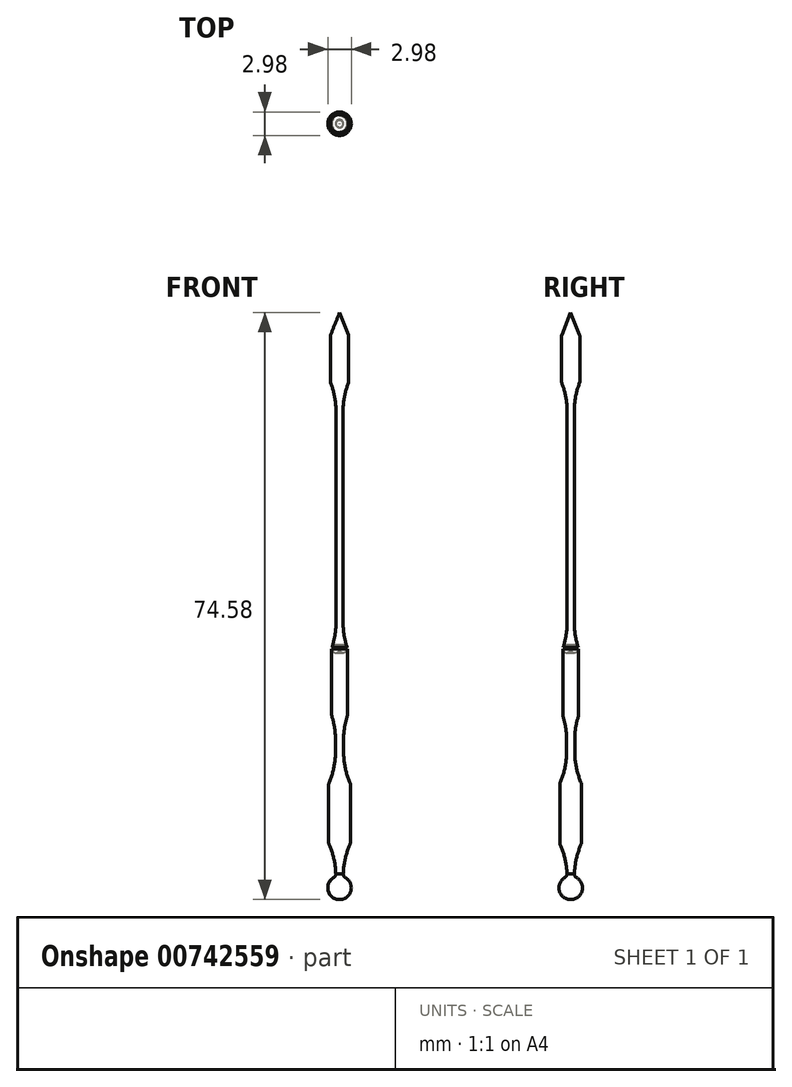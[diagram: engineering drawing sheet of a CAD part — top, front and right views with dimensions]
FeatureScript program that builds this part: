
annotation { "Feature Type Name" : "Feature", "Feature Type Description" : "" }
export const myFeature = defineFeature(function(context is Context, id is Id, definition is map)
    precondition{}
    {
        {
            var Q0;
            Q0=qCreatedBy(makeId("Front.planeOp"),FACE);
            var sketch = newSketch(context, id + "F0", { "sketchPlane" : qUnion([Q0])});
            skLineSegment(sketch, "E0", {"start": v(0, 9.94) * mm, "end": v(0.59, 8.47) * mm});
            skLineSegment(sketch, "E1", {"start": v(0.59, 8.47) * mm, "end": v(0.59, 5.32) * mm});
            skLineSegment(sketch, "E2", {"start": v(0.59, 5.32) * mm, "end": v(0.23, 5.32) * mm});
            skLineSegment(sketch, "E3", {"start": v(0.23, 5.32) * mm, "end": v(0.23, -11.17) * mm});
            skLineSegment(sketch, "E4", {"start": v(0.23, -11.17) * mm, "end": v(0.5, -11.17) * mm});
            skLineSegment(sketch, "E5", {"start": v(0.5, -11.17) * mm, "end": v(0.5, -15.88) * mm});
            skLineSegment(sketch, "E6", {"start": v(0.5, -15.88) * mm, "end": v(0.26, -15.88) * mm});
            skLineSegment(sketch, "E7", {"start": v(0.26, -15.88) * mm, "end": v(0.26, -19.8) * mm});
            skLineSegment(sketch, "E8", {"start": v(0.26, -19.8) * mm, "end": v(0.7, -19.8) * mm});
            skLineSegment(sketch, "E9", {"start": v(0.7, -19.8) * mm, "end": v(0.7, -23.98) * mm});
            skLineSegment(sketch, "E10", {"start": v(0.7, -23.98) * mm, "end": v(0.26, -23.98) * mm});
            skLineSegment(sketch, "E11", {"start": v(0.26, -23.98) * mm, "end": v(0.24, -25.9) * mm});
            skLineSegment(sketch, "E12", {"start": v(0, -26.6) * mm, "end": v(0, 9.94) * mm});
            skArc(sketch, "E13", {"start": v(0.24, -25.9) * mm, "mid": v(0.74, -26.72) * mm, "end": v(0, -27.35) * mm});
            skLineSegment(sketch, "E14", {"start": v(0, -26.6) * mm, "end": v(0, -27.35) * mm});
            skPoint(sketch, "E15.start.orphan", {"position": v(0.23, -26.6) * mm});
            skLineSegment(sketch, "E16", {"start": v(0, 9.94) * mm, "end": v(0, 12.06) * mm, "construction": true});
            skSolve(sketch);
        }
        {
            var Q0;
            Q0=makeQuery(id+"F0.imprint","IMPRINT",FACE,{"disambiguationData":[TD([[makeQuery(id+"F0.imprint","IMPRINT",EDGE,{"derivedFrom":sQuery(id+"F0.wireOp",EDGE,"E0")}),-1.0]])]});
            var Q1;
            Q1=sQuery(id+"F0.wireOp",EDGE,"E16");
            revolve(context, id + "F1", {"surfaceOperationType" : NewSurfaceOperationType.NEW, "entities" : qUnion([Q0]), "axis" : qUnion([Q1]), "revolveType" : RevolveType.FULL});
        }
        {
            var Q0;
            Q0=makeQuery(id+"F1.opRevolve","SWEPT_EDGE",EDGE,{"disambiguationData":[OSD([sQuery(id+"F0.wireOp",EDGE,"E1"),sQuery(id+"F0.wireOp",EDGE,"E2")])]});
            var Q1;
            Q1=makeQuery(id+"F1.opRevolve","SWEPT_EDGE",EDGE,{"disambiguationData":[OSD([sQuery(id+"F0.wireOp",EDGE,"E0"),sQuery(id+"F0.wireOp",EDGE,"E1")])]});
            var Q2;
            Q2=makeQuery(id+"F1.opRevolve","SWEPT_EDGE",EDGE,{"disambiguationData":[OSD([sQuery(id+"F0.wireOp",EDGE,"E4"),sQuery(id+"F0.wireOp",EDGE,"E5")])]});
            var Q3;
            Q3=makeQuery(id+"F1.opRevolve","SWEPT_EDGE",EDGE,{"disambiguationData":[OSD([sQuery(id+"F0.wireOp",EDGE,"E5"),sQuery(id+"F0.wireOp",EDGE,"E6")])]});
            var Q4;
            Q4=makeQuery(id+"F1.opRevolve","SWEPT_EDGE",EDGE,{"disambiguationData":[OSD([sQuery(id+"F0.wireOp",EDGE,"E8"),sQuery(id+"F0.wireOp",EDGE,"E9")])]});
            var Q5;
            Q5=makeQuery(id+"F1.opRevolve","SWEPT_EDGE",EDGE,{"disambiguationData":[OSD([sQuery(id+"F0.wireOp",EDGE,"E9"),sQuery(id+"F0.wireOp",EDGE,"E10")])]});
            var Q6;
            Q6=makeQuery(id+"F1.opRevolve","SWEPT_EDGE",EDGE,{"disambiguationData":[OSD([sQuery(id+"F0.wireOp",EDGE,"E11"),sQuery(id+"F0.wireOp",EDGE,"E13")])]});
            fillet(context, id + "F2", {"entities" : qUnion([Q0, Q1, Q2, Q3, Q4, Q5, Q6]), "radius" : 0.25 * mm, "tangentPropagation" : true, "allowEdgeOverflow" : false});
        }
        {
            var Q0;
            Q0=makeQuery(id+"F1.opRevolve","SWEPT_EDGE",EDGE,{"disambiguationData":[OSD([sQuery(id+"F0.wireOp",EDGE,"E10"),sQuery(id+"F0.wireOp",EDGE,"E11")])]});
            var Q1;
            Q1=makeQuery(id+"F1.opRevolve","SWEPT_EDGE",EDGE,{"disambiguationData":[OSD([sQuery(id+"F0.wireOp",EDGE,"E7"),sQuery(id+"F0.wireOp",EDGE,"E8")])]});
            var Q2;
            Q2=makeQuery(id+"F2.opFillet","BLEND_EDGE",EDGE,{"blendedFrom":[makeQuery(id+"F1.opRevolve","SWEPT_EDGE",EDGE,{"disambiguationData":[OSD([sQuery(id+"F0.wireOp",EDGE,"E5"),sQuery(id+"F0.wireOp",EDGE,"E6")])]}),makeQuery(id+"F1.opRevolve","SWEPT_FACE",FACE,{"disambiguationData":[OSD([sQuery(id+"F0.wireOp",EDGE,"E7")])]})],"blendedInto":[makeQuery(id+"F1.opRevolve","SWEPT_FACE",FACE,{"disambiguationData":[OSD([sQuery(id+"F0.wireOp",EDGE,"E7")])]})]});
            var Q3;
            Q3=makeQuery(id+"F1.opRevolve","SWEPT_EDGE",EDGE,{"disambiguationData":[OSD([sQuery(id+"F0.wireOp",EDGE,"E3"),sQuery(id+"F0.wireOp",EDGE,"E4")])]});
            var Q4;
            Q4=makeQuery(id+"F1.opRevolve","SWEPT_EDGE",EDGE,{"disambiguationData":[OSD([sQuery(id+"F0.wireOp",EDGE,"E2"),sQuery(id+"F0.wireOp",EDGE,"E3")])]});
            fillet(context, id + "F3", {"entities" : qUnion([Q0, Q1, Q2, Q3, Q4]), "radius" : 5.08 * mm, "tangentPropagation" : true, "allowEdgeOverflow" : false});
        }
        {
            var Q0;
            Q0=makeQuery(id+"F1.opRevolve","SWEPT_BODY",BODY,{"disambiguationData":[OSD([sQuery(id+"F0.wireOp",EDGE,"E0"),sQuery(id+"F0.wireOp",EDGE,"E1"),sQuery(id+"F0.wireOp",EDGE,"E2"),sQuery(id+"F0.wireOp",EDGE,"E3"),sQuery(id+"F0.wireOp",EDGE,"E4"),sQuery(id+"F0.wireOp",EDGE,"E5"),sQuery(id+"F0.wireOp",EDGE,"E6"),sQuery(id+"F0.wireOp",EDGE,"E7"),sQuery(id+"F0.wireOp",EDGE,"E8"),sQuery(id+"F0.wireOp",EDGE,"E9"),sQuery(id+"F0.wireOp",EDGE,"E10"),sQuery(id+"F0.wireOp",EDGE,"E11"),sQuery(id+"F0.wireOp",EDGE,"E12"),sQuery(id+"F0.wireOp",EDGE,"E13"),sQuery(id+"F0.wireOp",EDGE,"E14")])]});
            var Q1;
            Q1=qCreatedBy(makeId("Origin.pointOp"),VERTEX);
            var Q2;
            Q2=qCreatedBy(makeId("Origin.pointOp"),VERTEX);
            transform(context, id + "F4", {"entities" : qUnion([Q0]), "transformType" : TransformType.SCALE_UNIFORMLY, "scale" : 2, "scalePoint" : qUnion([Q2]), "makeCopy" : false});
        }
    });
